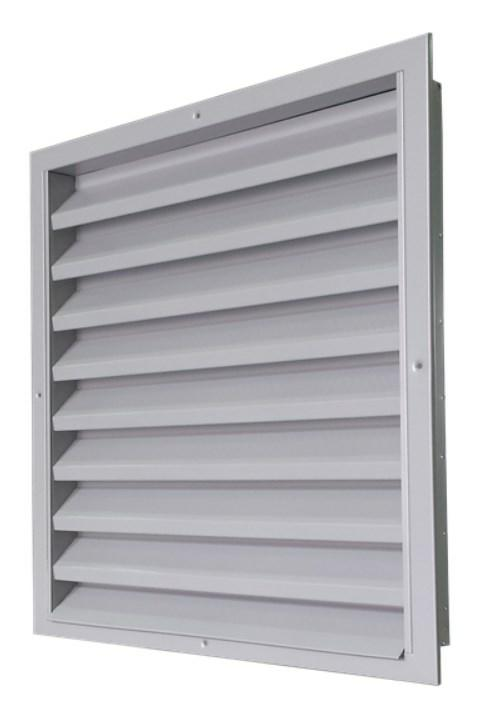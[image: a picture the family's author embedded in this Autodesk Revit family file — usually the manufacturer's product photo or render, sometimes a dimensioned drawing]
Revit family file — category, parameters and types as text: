
# Revit family: Czerpnia ścienna CzS-A
name_source: partatom
category: Terminale wentylacyjne
revit_build: Autodesk Revit 2018 (Build: 20190510_1515(x64)
units: mm (PartAtom-declared; Revit-internal decimal feet)

## family parameters
Numer OmniClass = 23.75.70.21.27.11
Oparty na płaszczyźnie roboczej = Nie
Punkt obliczania pomieszczeń = Nie
Tnij formami wycięć po wczytaniu = Nie
Typ części = Normalny
Tytuł OmniClass = Diffusers, Registers, and Grilles
Współdzielony = Nie
Wymiar okrągłego złącza = Użyj średnicy
Zawsze pionowo = Tak

## types (3) — shared parameters
Atest Higieniczny = HK/K/0522/02/2016
Deklaracja zgodności = 10/DZ/2020/K
IfcExportAs = IfcFlowTerminal
Karta katalogowa = https://www.sawpol.pl
Komentarze do typu = Czerpnia lub wyrzutnia powietrza
Maksymalna szerokość otworu montażowego modułu = 2800 mm  [stored 9.18635 ft]
Maksymalna wysokość otworu montażowego modułu = 1500 mm  [stored 4.92126 ft]
Minimalna szerokość otworu montażowego = 300 mm
Minimalna wysokość otworu montażowego = 300 mm
Model = CzS-A
Obraz typu = CZS-A.jpg
Producent = PPHU SAW-POL
URL = https://www.sawpol.pl
Wymiary - informacja = Jeżeli czerpnia przekracza maksymalne wymiary modułu (2800x1500) konieczne jest dzielenie produktu na moduły, których wymiary są ustalane indywidualnie

## per-type parameters (varying)
| type | H | L | Materiał | Materiał piór | Szerokość otworu montażowego | Szerokość wlotu | Wykonanie aluminium | Wykonanie stal nierdzewna | Wykonanie stal ocynkowana | Wysokość otworu montażowego | Wysokość wlotu |
| OC | 1000 mm  [stored 3.28084 ft] | 1000 mm  [stored 3.28084 ft] | SAW_POL Stal ocynkowana | SAW_POL Stal ocynkowana | 1000 mm  [stored 3.28084 ft] | 990 mm  [stored 3.24803 ft] | Nie | Nie | Tak | 1000 mm  [stored 3.28084 ft] | 990 mm  [stored 3.24803 ft] |
| AL | 1000 mm  [stored 3.28084 ft] | 1000 mm  [stored 3.28084 ft] | SAW_POL Aluminium | SAW_POL Aluminium | 1000 mm  [stored 3.28084 ft] | 990 mm  [stored 3.24803 ft] | Tak | Nie | Nie | 1000 mm  [stored 3.28084 ft] | 990 mm  [stored 3.24803 ft] |
| KO | 1500 mm  [stored 4.92126 ft] | 1500 mm  [stored 4.92126 ft] | SAW-POL Stal nierdzewna | SAW-POL Stal nierdzewna | 1500 mm  [stored 4.92126 ft] | 1490 mm  [stored 4.88845 ft] | Nie | Tak | Nie | 1500 mm  [stored 4.92126 ft] | 1490 mm  [stored 4.88845 ft] |

note: [stored X ft] marks values corroborated as IEEE doubles in the binary element streams (Revit-internal decimal feet)
